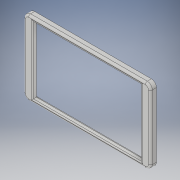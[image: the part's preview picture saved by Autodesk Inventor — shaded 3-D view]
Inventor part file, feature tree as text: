
AUTODESK INVENTOR PART (.ipt)
format: ipt  version: 2018 (Build 220112000, 112)  size: 222,720 bytes
history: native  units: in
note: dims shown in document units (in); Inventor stores cm internally (conversion verified against a paired STEP export)
features: extrude x4, sketch x4, fillet x3, chamfer x1
ambient origin geometry x8: Origin, YZ Plane, XZ Plane, XY Plane, X Axis, Y Axis, Z Axis, Center Point
bodies: Solid1 (feature_tree)
feature tree (12):
  extrude  "Extrusion1"  Depth=3.9665in
  extrude  "Extrusion2"  Depth=7.5984in
  fillet  "Fillet2"  Radius=0.125in
  extrude  "Extrusion3"  Depth=0.125in
  fillet  "Fillet3"  Radius=0.125in
  chamfer  "Chamfer1"  Distance=0.125in
  fillet  "Fillet4"  Radius=0.125in
  extrude  "Extrusion4"  Depth=0.315in
  sketch  "Sketch1"  dims[d0=6.5098in d1=3.9665in]
  sketch  "Sketch2"  dims[d2=4.3701in d3=7.5984in d4=0.125in d5=0.0in]
  sketch  "Sketch3"  dims[d7=0.125in d8=0.125in d9=0.125in d10=0.0in]
  sketch  "Sketch4"  dims[d11=0.315in d12=0.125in d13=0.125in d14=0.315in d15=0.315in d16=0.25in d17=0.0in d18=0.125in d19=0.125in d20=0.125in d21=45.0deg d22=0.125in d25=0.0625in d26=0.0625in d27=0.0625in d28=0.0625in d29=0.0625in d30=0.0625in d31=0.0625in d32=0.0625in d33=0.25in d34=0.0in]
